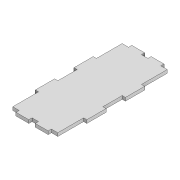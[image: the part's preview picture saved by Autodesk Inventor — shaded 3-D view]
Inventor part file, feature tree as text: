
AUTODESK INVENTOR PART (.ipt)
format: ipt  version: 2022 (Build 260153000, 153)  size: 122,368 bytes
history: native  units: mm
features: extrude x1, sketch x1
ambient origin geometry x8: Origin, YZ Plane, XZ Plane, XY Plane, X Axis, Y Axis, Z Axis, Center Point
bodies: Solid1 (feature_tree)
feature tree (2):
  extrude  "Extrusion1"  Depth=70.0mm
  sketch  "Sketch1"  dims[d0=170.0mm d1=70.0mm d2=5.0mm d3=30.0mm d4=5.0mm d5=30.0mm d6=30.0mm d7=15.0mm d8=20.0mm d9=20.0mm d10=5.0mm d11=5.0mm d12=10.0mm d13=5.0mm d14=5.0mm d15=0.0mm]
